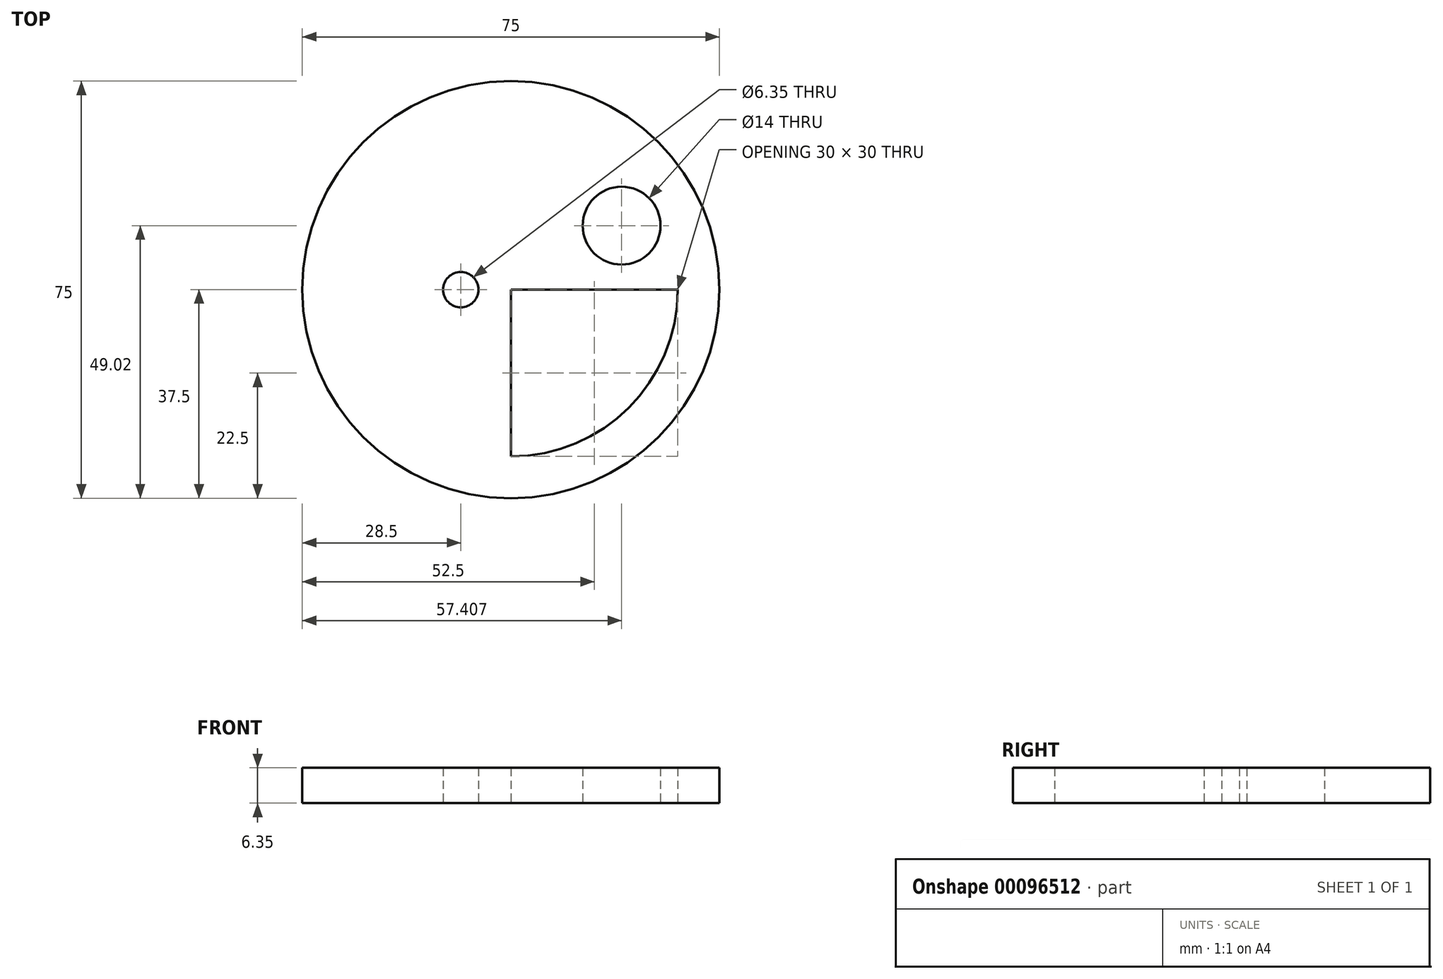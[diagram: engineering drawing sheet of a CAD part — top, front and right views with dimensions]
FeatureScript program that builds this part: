
annotation { "Feature Type Name" : "Feature", "Feature Type Description" : "" }
export const myFeature = defineFeature(function(context is Context, id is Id, definition is map)
    precondition{}
    {
        {
            var Q0;
            Q0=qCreatedBy(makeId("Top.planeOp"),FACE);
            var sketch = newSketch(context, id + "F0", { "sketchPlane" : qUnion([Q0])});
            skCircle(sketch, "E0", {"center": v(0, 0) * mm, "radius": 37.5 * mm});
            skCircle(sketch, "E1", {"center": v(-9, 0) * mm, "radius": 3.18 * mm});
            skArc(sketch, "E2", {"start": v(0, -30) * mm, "mid": v(21.21, -21.21) * mm, "end": v(30, 0) * mm});
            skLineSegment(sketch, "E3", {"start": v(0, 0) * mm, "end": v(0, -30) * mm});
            skLineSegment(sketch, "E4", {"start": v(0, 0) * mm, "end": v(30, 0) * mm});
            skCircle(sketch, "E5", {"center": v(19.9, 11.52) * mm, "radius": 7 * mm});
            skSolve(sketch);
        }
        {
            var Q0;
            Q0 = qSketchRegion(id + "F0", true);
            extrude(context, id + "F1", {"entities" : qUnion([Q0]), "depth" : 6.35 * mm});
        }
    });
